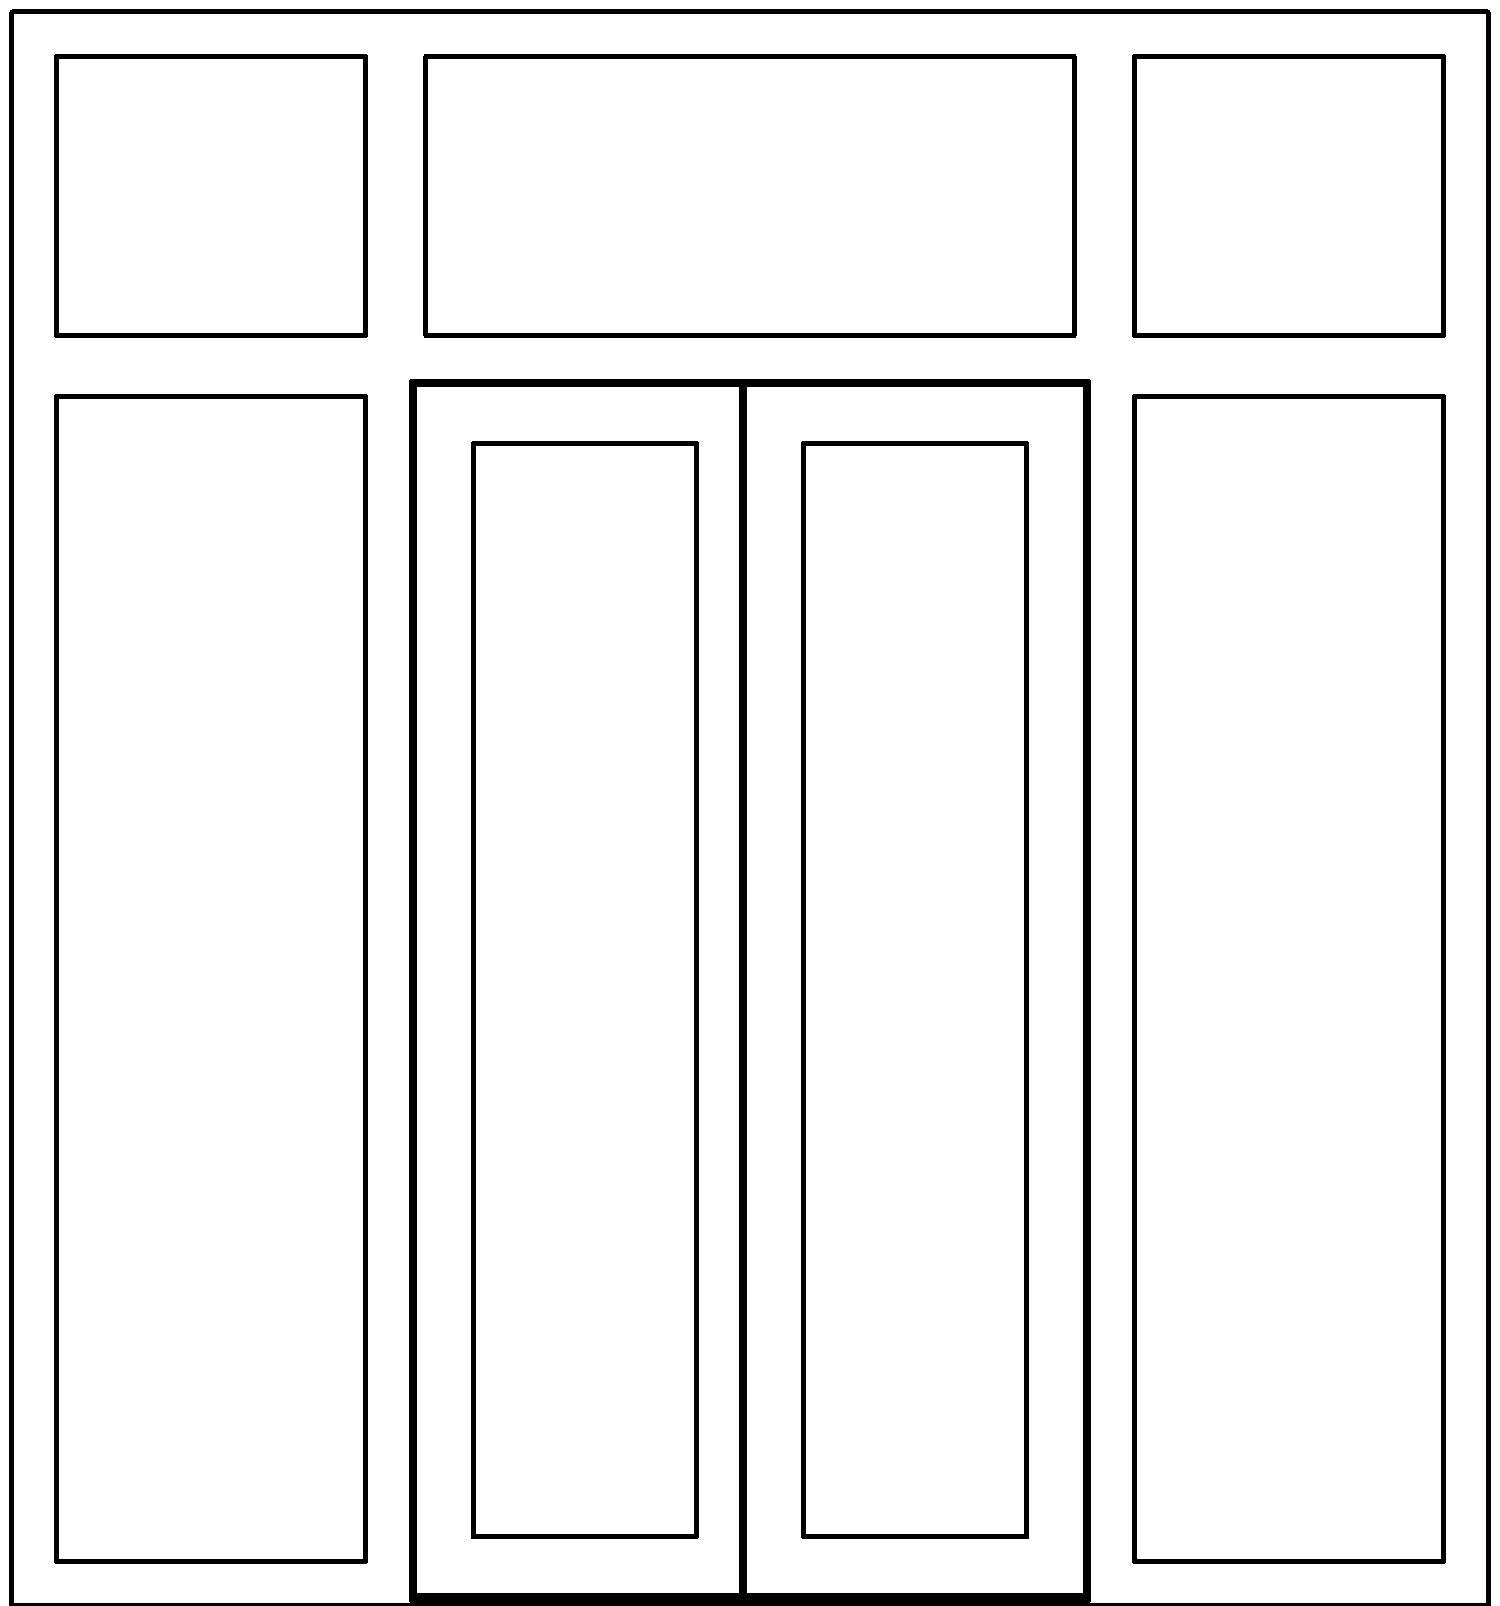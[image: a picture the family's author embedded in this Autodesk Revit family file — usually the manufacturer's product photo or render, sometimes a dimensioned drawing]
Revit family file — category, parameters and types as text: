
# Revit family: Входная группа.Alumark_двупольная_S50
name_source: partatom
category: Двери
revit_build: Autodesk Revit 2017 (Build: 20190508_0315(x64)
units: mm (PartAtom-declared; Revit-internal decimal feet)

## family parameters
Всегда вертикально = Да
Заголовок OmniClass = Doors
Номер OmniClass = 23.30.10.00
Общий = Нет
Основа = Стена
При загрузке вырезать с полостями = Нет
Точка расчета площади = Нет

## types (2) — shared parameters
ADSK_Завод-изготовитель = ТБМ
ADSK_Обозначение = ГОСТ 23747-2015
URL = http://www.tbm.ru
sp_energy = Энергосберегающие стекла
sp_gaz = Заполненный газом
sp_standart = Обычный стеклопакет
Аналитическая конструкция = Застеклённая створчатая дверь, металлическая рама с двумя стеклами
Высота импоста = 800 мм
Дверь с цоколем = Нет
Дверь ширина = 1400 мм
Заполнение стеклопакета = Обычный стеклопакет
Изготовитель = ТБМ
Изображение типоразмера = схема_входная группа_двупольная.png
Импост двери = Нет
Коэффициент теплопередачи (U) = 4.2812 Вт/(м²·K)
Материал остекления = <По категории>
Материал профилей = <По категории>
Материал фурнитуры = <По категории>
Одинаковые полотна = Да
Окно высота = 300 мм
Описание = Дверь Проем ТБМ
Примерная высота = 2380 мм
Примерная ширина = 2360 мм
Равные окна сбоку = Да
Разработчик = ООО ПРОРУБИМ
Разработчик (телефон) = +7(495)649-85-43
ТБМ_Артикул_Импост = ALM252304
ТБМ_Артикул_Крепление порога = ALM744630
ТБМ_Артикул_Подкладка под СП = ALM744307
ТБМ_Артикул_Порог = ALM752630
ТБМ_Артикул_Рама = ALM252102
ТБМ_Артикул_Распорный штифт = ALM885014
ТБМ_Артикул_Угловой соединитель рамы = ALM752502
ТБМ_Артикул_Угловой соединитель створки = ALM770421
ТБМ_Артикул_Уголок жесткости = ALM770426
ТБМ_Артикул_Уплотнитель внутренний = ALM770207
ТБМ_Артикул_Уплотнитель наружный = ALM770004
ТБМ_Артикул_Уплотнитель порога = ELM0336
ТБМ_Артикул_Уплотнитель притвора = ALM770020
ТБМ_Артикул_Штапик = ALM200010
ТБМ_Длина_Импост = 6866 мм
ТБМ_Длина_Порог = 1296 мм
ТБМ_Длина_Притвор = 5456 мм
ТБМ_Длина_Рама = 8038 мм
ТБМ_Длина_Створка = 7376 мм
ТБМ_Длина_Створка 2 = 2024 мм
ТБМ_Длина_Уплотнитель внутренний = 25128 мм
ТБМ_Длина_Уплотнитель наружный = 25128 мм
ТБМ_Длина_Уплотнитель порога = 1296 мм
ТБМ_Длина_Уплотнитель притвора = 14752 мм
ТБМ_Длина_Штапик = 25128 мм
ТБМ_Количество_Крепление порога = 1
ТБМ_Количество_Подкладка под СП = 28
ТБМ_Количество_Распорный штифт = 32
ТБМ_Количество_Т-соединитель цоколя = 5
ТБМ_Количество_Угловой соединитель рамы = 4
ТБМ_Количество_Угловой соединитель створки = 12
ТБМ_Количество_Уголок жесткости = 14
ТБМ_Площадь стеклопакета = 3.94 м²
Термостойкость = 0.2336 (м²·K)/Вт
Тип стеклопакета = 24мм 1-камерный
Толщина = 50 мм
Функция = Наружные слои
Ширина окна слева = 960 мм
Ширина створки слева = 700 мм
Ширина створки справа = 700 мм
автоматика = Фурнитура с автоматикой
импост_ширина = 86 мм
импост_ширина_05 = 43 мм
окно_слева_ширина = 480 мм
окно_справа_ширина = 480 мм
рама_ширина = 72 мм
сп_16_мм = 16мм 1-камерный
сп_24_мм = 24мм 1-камерный
створка_справа_ширина = 700 мм
створка_ширина = 94 мм
таблица выбора = каталог ТБМ двупольная дверь S44
фурнитура_высота = 2123 мм
штапик_толщина = 17 мм
zero-valued in all types: Коэффициент теплопритока от солнечного излучения, Пропускание видимого света, ТБМ_Длина_Притвор цоколя, ТБМ_Длина_Цоколь, Ширина окна справа

## per-type parameters (varying)
| type | ADSK_Наименование | Открывание внутрь | Открывание наружу | ТБМ_Артикул_Притвор | ТБМ_Артикул_Створка | ТБМ_Артикул_Створка 2 | номер профиля |
| 1160х2380 Открывание наружу (СП 24мм Обычный) | ДАН О Оп Р (Однокамерный стеклопакет 24 мм) | Нет | Да | ALM252382 | ALM252281 | ALM252280 | 11101 |
| 1160х2380 Открывание внутрь (СП 24мм Обычный) | ДАВ О Оп Р (Однокамерный стеклопакет 24 мм) | Да | Нет | ALM462805 | ALM252280 | ALM252281 | 21101 |
